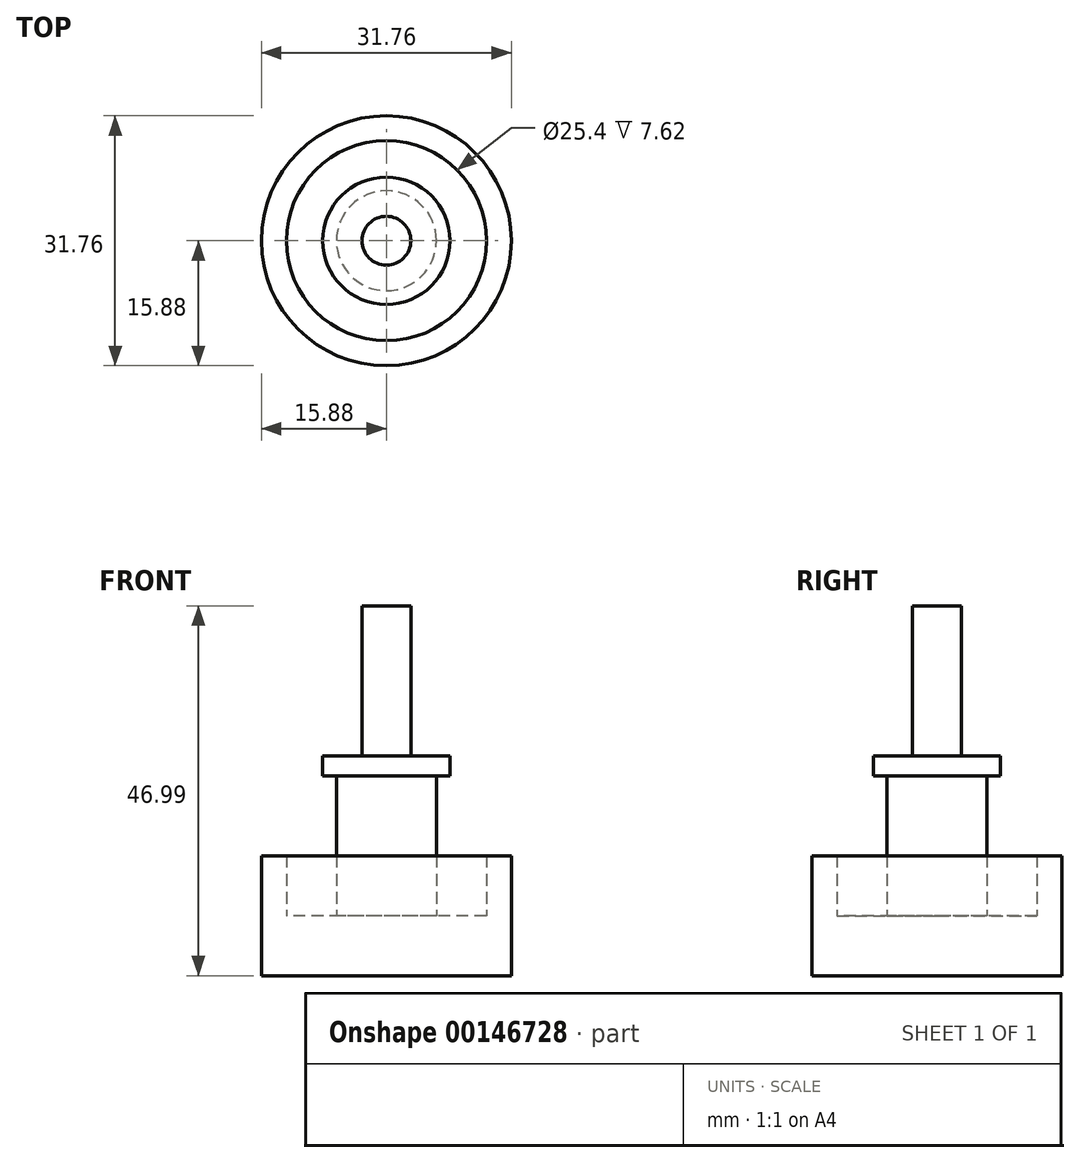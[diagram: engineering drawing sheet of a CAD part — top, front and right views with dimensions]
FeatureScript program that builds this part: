
annotation { "Feature Type Name" : "Feature", "Feature Type Description" : "" }
export const myFeature = defineFeature(function(context is Context, id is Id, definition is map)
    precondition{}
    {
        {
            var Q0;
            Q0=qCreatedBy(makeId("Top.planeOp"),FACE);
            var sketch = newSketch(context, id + "F0", { "sketchPlane" : qUnion([Q0])});
            skCircle(sketch, "E0", {"center": v(0, 0) * mm, "radius": 15.88 * mm});
            skCircle(sketch, "E1", {"center": v(0, 0) * mm, "radius": 12.7 * mm});
            skCircle(sketch, "E2", {"center": v(0, 0) * mm, "radius": 6.35 * mm});
            skSolve(sketch);
        }
        {
            var Q0;
            Q0=makeQuery(id+"F0.imprint","IMPRINT",FACE,{"disambiguationData":[TD([[makeQuery(id+"F0.imprint","IMPRINT",EDGE,{"derivedFrom":sQuery(id+"F0.wireOp",EDGE,"E1")}),1.0]])]});
            extrude(context, id + "F1", {"entities" : qUnion([Q0]), "depth" : 7.62 * mm});
        }
        {
            var Q0;
            Q0=makeQuery(id+"F0.imprint","IMPRINT",FACE,{"disambiguationData":[TD([[makeQuery(id+"F0.imprint","IMPRINT",EDGE,{"derivedFrom":sQuery(id+"F0.wireOp",EDGE,"E0")}),1.0]])]});
            extrude(context, id + "F2", {"entities" : qUnion([Q0]), "operationType" : NewBodyOperationType.ADD, "depth" : 15.24 * mm});
        }
        {
            var Q0;
            Q0=makeQuery(id+"F0.imprint","IMPRINT",FACE,{"disambiguationData":[TD([[makeQuery(id+"F0.imprint","IMPRINT",EDGE,{"derivedFrom":sQuery(id+"F0.wireOp",EDGE,"E2")}),1.0]])]});
            extrude(context, id + "F3", {"entities" : qUnion([Q0]), "operationType" : NewBodyOperationType.ADD, "depth" : 27.94 * mm});
        }
        {
            var Q0;
            Q0=makeQuery(id+"F3.opExtrude","CAP_FACE",FACE,{"disambiguationData":[OSD([sQuery(id+"F0.wireOp",EDGE,"E2")])],"isStart":false});
            var sketch = newSketch(context, id + "F4", { "sketchPlane" : qUnion([Q0])});
            skCircle(sketch, "E3", {"center": v(0, 0) * mm, "radius": 25.4 * mm});
            skLineSegment(sketch, "E4", {"start": v(-20.32, -15.24) * mm, "end": v(20.32, -15.24) * mm});
            skLineSegment(sketch, "E5", {"start": v(-20.32, -15.24) * mm, "end": v(0, 0) * mm});
            skLineSegment(sketch, "E6", {"start": v(20.32, -15.24) * mm, "end": v(0, 0) * mm});
            skCircle(sketch, "E7", {"center": v(0, 0) * mm, "radius": 19.05 * mm});
            skCircle(sketch, "E8", {"center": v(0, 0) * mm, "radius": 22.86 * mm});
            skCircle(sketch, "E9", {"center": v(0, 0) * mm, "radius": 16.51 * mm});
            skLineSegment(sketch, "E10", {"start": v(20.32, -15.24) * mm, "end": v(8.94, 23.77) * mm});
            skLineSegment(sketch, "E11", {"start": v(8.94, 23.77) * mm, "end": v(0, 0) * mm});
            skLineSegment(sketch, "E12", {"start": v(0, 0) * mm, "end": v(-15.24, 11.43) * mm});
            skLineSegment(sketch, "E13", {"start": v(0, 0) * mm, "end": v(-17, 8.6) * mm});
            skCircle(sketch, "E14", {"center": v(0, 0) * mm, "radius": 6.35 * mm});
            skLineSegment(sketch, "E15", {"start": v(0, 0) * mm, "end": v(11.58, 11.77) * mm});
            skCircle(sketch, "E16", {"center": v(0, 0) * mm, "radius": 3.11 * mm});
            skCircle(sketch, "E17", {"center": v(0, 0) * mm, "radius": 8.09 * mm});
            skSolve(sketch);
        }
        {
            var Q0;
            {var subQ1=sQuery(id+"F4.wireOp",EDGE,"E6");var subQ3=sQuery(id+"F4.wireOp",EDGE,"E16");var subQ4=makeQuery(id+"F4.imprint","INTERSECT",VERTEX,{"derivedFrom":[subQ1,subQ3]});Q0=makeQuery(id+"F4.imprint","IMPRINT",FACE,{"disambiguationData":[TD([[makeQuery(id+"F4.imprint","IMPRINT",EDGE,{"disambiguationData":[TD([[subQ4,-1.0]])],"derivedFrom":subQ3}),1.0]])]});}
            var Q1;
            {var subQ1=sQuery(id+"F4.wireOp",EDGE,"E11");var subQ3=sQuery(id+"F4.wireOp",EDGE,"E16");var subQ4=makeQuery(id+"F4.imprint","INTERSECT",VERTEX,{"derivedFrom":[subQ1,subQ3]});Q1=makeQuery(id+"F4.imprint","IMPRINT",FACE,{"disambiguationData":[TD([[makeQuery(id+"F4.imprint","IMPRINT",EDGE,{"disambiguationData":[TD([[subQ4,1.0]])],"derivedFrom":subQ3}),1.0]])]});}
            var Q2;
            {var subQ1=sQuery(id+"F4.wireOp",EDGE,"E5");var subQ3=sQuery(id+"F4.wireOp",EDGE,"E16");var subQ4=makeQuery(id+"F4.imprint","INTERSECT",VERTEX,{"derivedFrom":[subQ1,subQ3]});Q2=makeQuery(id+"F4.imprint","IMPRINT",FACE,{"disambiguationData":[TD([[makeQuery(id+"F4.imprint","IMPRINT",EDGE,{"disambiguationData":[TD([[subQ4,1.0]])],"derivedFrom":subQ3}),1.0]])]});}
            var Q3;
            {var subQ1=sQuery(id+"F4.wireOp",EDGE,"E12");var subQ3=sQuery(id+"F4.wireOp",EDGE,"E16");var subQ4=makeQuery(id+"F4.imprint","INTERSECT",VERTEX,{"derivedFrom":[subQ1,subQ3]});Q3=makeQuery(id+"F4.imprint","IMPRINT",FACE,{"disambiguationData":[TD([[makeQuery(id+"F4.imprint","IMPRINT",EDGE,{"disambiguationData":[TD([[subQ4,-1.0]])],"derivedFrom":subQ3}),1.0]])]});}
            var Q4;
            {var subQ1=sQuery(id+"F4.wireOp",EDGE,"E11");var subQ3=sQuery(id+"F4.wireOp",EDGE,"E16");var subQ4=makeQuery(id+"F4.imprint","INTERSECT",VERTEX,{"derivedFrom":[subQ1,subQ3]});Q4=makeQuery(id+"F4.imprint","IMPRINT",FACE,{"disambiguationData":[TD([[makeQuery(id+"F4.imprint","IMPRINT",EDGE,{"disambiguationData":[TD([[subQ4,-1.0]])],"derivedFrom":subQ3}),1.0]])]});}
            var Q5;
            {var subQ1=sQuery(id+"F4.wireOp",EDGE,"E5");var subQ3=sQuery(id+"F4.wireOp",EDGE,"E16");var subQ4=makeQuery(id+"F4.imprint","INTERSECT",VERTEX,{"derivedFrom":[subQ1,subQ3]});Q5=makeQuery(id+"F4.imprint","IMPRINT",FACE,{"disambiguationData":[TD([[makeQuery(id+"F4.imprint","IMPRINT",EDGE,{"disambiguationData":[TD([[subQ4,-1.0]])],"derivedFrom":subQ3}),1.0]])]});}
            extrude(context, id + "F5", {"entities" : qUnion([Q0, Q1, Q2, Q3, Q4, Q5]), "operationType" : NewBodyOperationType.ADD, "depth" : 19.05 * mm});
        }
        {
            var Q0;
            {var subQ0=sQuery(id+"F4.wireOp",EDGE,"E17");var subQ1=sQuery(id+"F4.wireOp",EDGE,"E5");var subQ2=makeQuery(id+"F4.imprint","INTERSECT",VERTEX,{"derivedFrom":[subQ1,subQ0]});Q0=makeQuery(id+"F4.imprint","IMPRINT",FACE,{"disambiguationData":[TD([[makeQuery(id+"F4.imprint","IMPRINT",EDGE,{"disambiguationData":[TD([[subQ2,-1.0]])],"derivedFrom":subQ1}),1.0]])]});}
            var Q1;
            {var subQ0=sQuery(id+"F4.wireOp",EDGE,"E14");var subQ1=sQuery(id+"F4.wireOp",EDGE,"E12");var subQ2=makeQuery(id+"F4.imprint","INTERSECT",VERTEX,{"derivedFrom":[subQ1,subQ0]});Q1=makeQuery(id+"F4.imprint","IMPRINT",FACE,{"disambiguationData":[TD([[makeQuery(id+"F4.imprint","IMPRINT",EDGE,{"disambiguationData":[TD([[subQ2,-1.0]])],"derivedFrom":subQ1}),1.0]])]});}
            var Q2;
            {var subQ0=sQuery(id+"F4.wireOp",EDGE,"E17");var subQ1=sQuery(id+"F4.wireOp",EDGE,"E11");var subQ2=makeQuery(id+"F4.imprint","INTERSECT",VERTEX,{"derivedFrom":[subQ1,subQ0]});Q2=makeQuery(id+"F4.imprint","IMPRINT",FACE,{"disambiguationData":[TD([[makeQuery(id+"F4.imprint","IMPRINT",EDGE,{"disambiguationData":[TD([[subQ2,-1.0]])],"derivedFrom":subQ1}),-1.0]])]});}
            var Q3;
            {var subQ0=sQuery(id+"F4.wireOp",EDGE,"E17");var subQ1=sQuery(id+"F4.wireOp",EDGE,"E11");var subQ2=makeQuery(id+"F4.imprint","INTERSECT",VERTEX,{"derivedFrom":[subQ1,subQ0]});Q3=makeQuery(id+"F4.imprint","IMPRINT",FACE,{"disambiguationData":[TD([[makeQuery(id+"F4.imprint","IMPRINT",EDGE,{"disambiguationData":[TD([[subQ2,-1.0]])],"derivedFrom":subQ1}),1.0]])]});}
            var Q4;
            {var subQ0=sQuery(id+"F4.wireOp",EDGE,"E17");var subQ1=sQuery(id+"F4.wireOp",EDGE,"E6");var subQ2=makeQuery(id+"F4.imprint","INTERSECT",VERTEX,{"derivedFrom":[subQ1,subQ0]});Q4=makeQuery(id+"F4.imprint","IMPRINT",FACE,{"disambiguationData":[TD([[makeQuery(id+"F4.imprint","IMPRINT",EDGE,{"disambiguationData":[TD([[subQ2,-1.0]])],"derivedFrom":subQ1}),-1.0]])]});}
            var Q5;
            {var subQ0=sQuery(id+"F4.wireOp",EDGE,"E17");var subQ1=sQuery(id+"F4.wireOp",EDGE,"E6");var subQ2=makeQuery(id+"F4.imprint","INTERSECT",VERTEX,{"derivedFrom":[subQ1,subQ0]});Q5=makeQuery(id+"F4.imprint","IMPRINT",FACE,{"disambiguationData":[TD([[makeQuery(id+"F4.imprint","IMPRINT",EDGE,{"disambiguationData":[TD([[subQ2,-1.0]])],"derivedFrom":subQ1}),-1.0]])]});}
            var Q6;
            {var subQ0=sQuery(id+"F4.wireOp",EDGE,"E17");var subQ1=sQuery(id+"F4.wireOp",EDGE,"E5");var subQ2=makeQuery(id+"F4.imprint","INTERSECT",VERTEX,{"derivedFrom":[subQ1,subQ0]});Q6=makeQuery(id+"F4.imprint","IMPRINT",FACE,{"disambiguationData":[TD([[makeQuery(id+"F4.imprint","IMPRINT",EDGE,{"disambiguationData":[TD([[subQ2,-1.0]])],"derivedFrom":subQ1}),-1.0]])]});}
            extrude(context, id + "F6", {"entities" : qUnion([Q0, Q1, Q2, Q3, Q4, Q5, Q6]), "operationType" : NewBodyOperationType.ADD, "oppositeDirection" : true, "depth" : 2.54 * mm});
        }
    });
